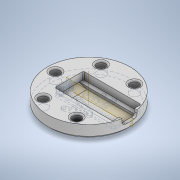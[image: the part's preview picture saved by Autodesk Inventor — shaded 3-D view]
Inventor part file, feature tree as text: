
AUTODESK INVENTOR PART (.ipt)
format: ipt  version: 2021 (Build 250183000, 183)  size: 878,080 bytes
history: native  units: in
note: dims shown in document units (in); Inventor stores cm internally (conversion verified against a paired STEP export)
features: extrude x7, sketch x7, fillet x3, chamfer x2, other x1, plane x1, pattern_circular x1
ambient origin geometry x8: Origin, YZ Plane, XZ Plane, XY Plane, X Axis, Y Axis, Z Axis, Center Point
bodies: Solid1 (feature_tree)
feature tree (22):
  extrude  "Extrusion1"  Depth=0.315in TaperAngle=0.0deg
  chamfer  "Chamfer2"  Distance=0.1811in
  extrude  "Extrusion2"  Depth=0.1654in
  extrude  "Extrusion3"  Depth=0.2205in
  other  "Work Axis1"
  plane  "Work Plane1"
  extrude  "Extrusion5"  Depth=0.2047in TaperAngle=0.0deg
  extrude  "Extrusion4"  Depth=0.8268in
  fillet  "Fillet4"  Radius=0.3539in
  pattern_circular  "Circular Pattern2"  [2 undecoded]
  chamfer  "Chamfer3"  Distance=1.4in
  fillet  "Fillet7"  Radius=0.25in
  extrude  "Extrusion9"  TaperAngle=0.0deg  [1 undecoded]
  extrude  "Extrusion10"  Depth=0.063in TaperAngle=0.0deg
  fillet  "Fillet9"  Radius=0.1654in
  sketch  "Sketch1"  dims[d0=2.0472in d3=0.315in d4=0.0in]
  sketch  "Sketch2"  dims[d5=1.4315in]
  sketch  "Sketch3"  dims[d6=0.7079in]
  sketch  "Sketch4"  dims[d7=0.3539in]
  sketch  "Sketch7"  dims[d8=0.4882in d9=0.1811in d10=0.0in]
  sketch  "Sketch12"  dims[d11=0.0in d14=0.1654in]
  sketch  "Sketch13"  dims[d15=0.0in d16=0.0in d17=0.2205in d18=0.2047in d19=0.0in d23=0.8268in d24=0.3539in d28=0.5in d29=1.4in d30=0.25in d31=0.0in d32=0.063in d33=0.0in d44=0.1654in d47=0.0315in d48=0.0in d49=0.0in d51=0.0in d54=0.063in d55=0.0in d56=45.0deg d58=0.0394in d59=0.1181in d60=1.9685in d61=240.0deg d63=0.0591in d64=0.1969in d65=45.0deg d72=0.0315in d79=0.1039in d80=0.9517in d81=0.4759in d82=0.9728in d83=0.4864in d84=0.0394in d85=0.0in d86=0.547in d87=0.2735in d88=0.1575in d89=0.0in d90=0.0787in d91=0.0197in d92=0.0344in d93=0.0197in d94=0.0344in]
note: 3 required parameter values undecoded (feature->parameter linkage not recoverable at this tier; creation-order binding heuristic only, values carry confidence <= 0.55)
